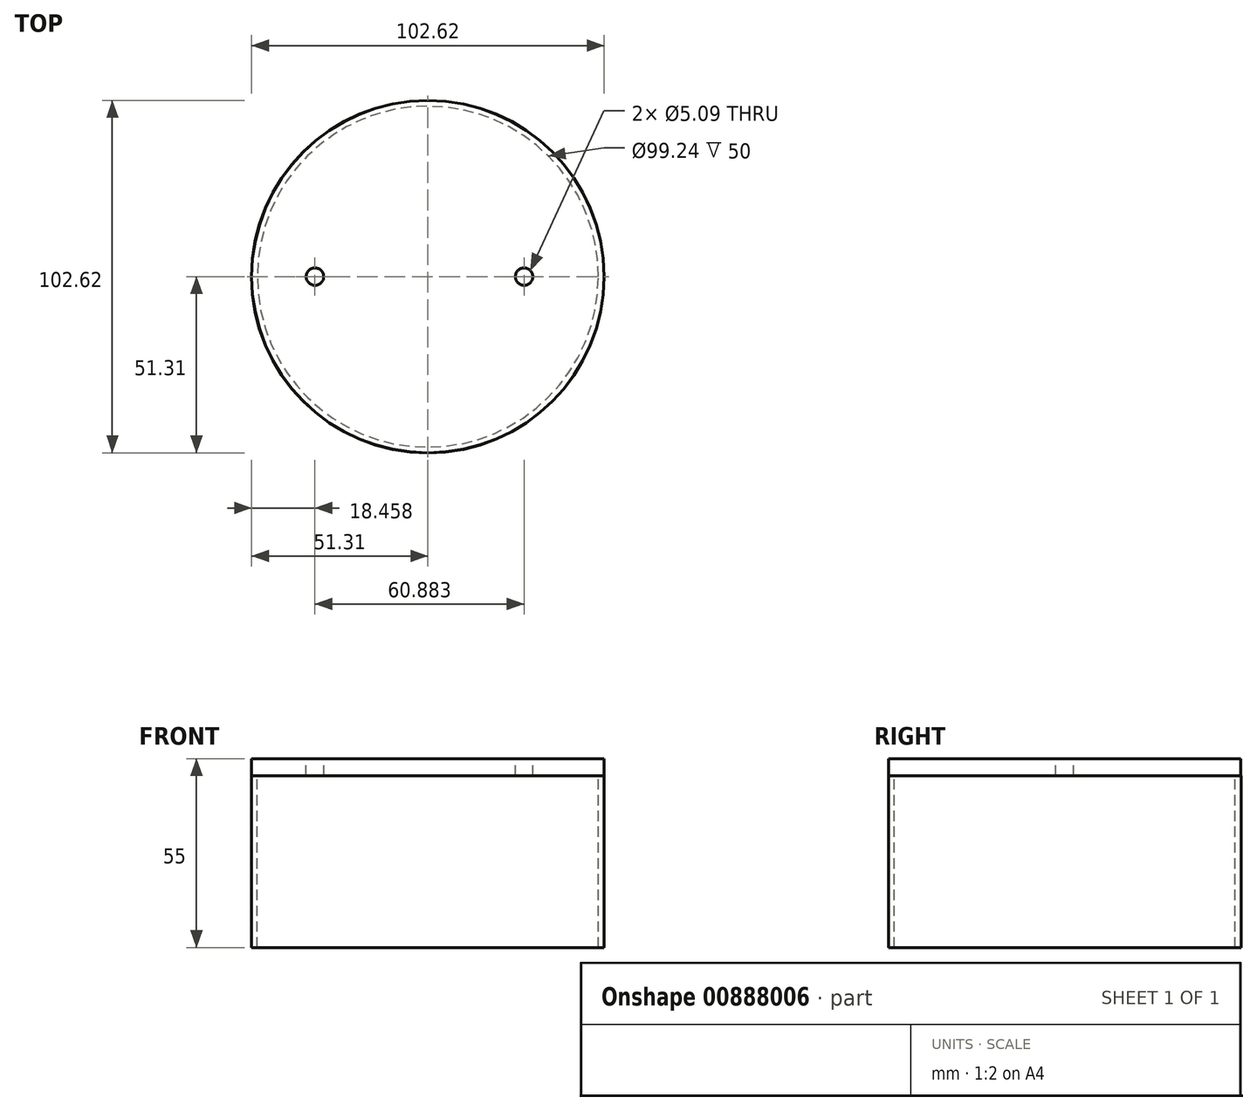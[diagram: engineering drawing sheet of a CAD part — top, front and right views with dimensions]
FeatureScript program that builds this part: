
annotation { "Feature Type Name" : "Feature", "Feature Type Description" : "" }
export const myFeature = defineFeature(function(context is Context, id is Id, definition is map)
    precondition{}
    {
        {
            var Q0;
            Q0=qCreatedBy(makeId("Top.planeOp"),FACE);
            var sketch = newSketch(context, id + "F0", { "sketchPlane" : qUnion([Q0])});
            skCircle(sketch, "E0", {"center": v(0, 0) * mm, "radius": 51.31 * mm});
            skCircle(sketch, "E1", {"center": v(0, 0) * mm, "radius": 49.62 * mm});
            skSolve(sketch);
        }
        {
            var Q0;
            Q0=makeQuery(id+"F0.imprint","IMPRINT",FACE,{"disambiguationData":[TD([[makeQuery(id+"F0.imprint","IMPRINT",EDGE,{"derivedFrom":sQuery(id+"F0.wireOp",EDGE,"E0")}),1.0]])]});
            extrude(context, id + "F1", {"entities" : qUnion([Q0]), "oppositeDirection" : true, "depth" : 50 * mm, "offsetDistance" : 25 * mm});
        }
        {
            var Q0;
            Q0=qCreatedBy(makeId("Top.planeOp"),FACE);
            var sketch = newSketch(context, id + "F2", { "sketchPlane" : qUnion([Q0])});
            skCircle(sketch, "E2", {"center": v(0, 0) * mm, "radius": 51.28 * mm});
            skSolve(sketch);
        }
        {
            var Q0;
            Q0 = qSketchRegion(id + "F2", true);
            extrude(context, id + "F3", {"entities" : qUnion([Q0]), "operationType" : NewBodyOperationType.ADD, "depth" : 5 * mm, "offsetDistance" : 25 * mm});
        }
        {
            var Q0;
            Q0=makeQuery(id+"F3.opExtrude","CAP_FACE",FACE,{"disambiguationData":[OSD([sQuery(id+"F2.wireOp",EDGE,"E2")])],"isStart":false});
            extrude(context, id + "F4", {"entities" : qUnion([Q0]), "operationType" : NewBodyOperationType.ADD, "oppositeDirection" : true, "depth" : 5 * mm, "offsetDistance" : 25 * mm});
        }
        {
            var Q0;
            Q0=makeQuery(id+"F3.opExtrude","CAP_FACE",FACE,{"disambiguationData":[OSD([sQuery(id+"F2.wireOp",EDGE,"E2")])],"isStart":false});
            var sketch = newSketch(context, id + "F5", { "sketchPlane" : qUnion([Q0])});
            skCircle(sketch, "E3", {"center": v(-32.85, 0) * mm, "radius": 2.55 * mm});
            skCircle(sketch, "E4", {"center": v(28.03, 0) * mm, "radius": 2.55 * mm});
            skSolve(sketch);
        }
        {
            var Q0;
            Q0 = qSketchRegion(id + "F5", true);
            extrude(context, id + "F6", {"entities" : qUnion([Q0]), "operationType" : NewBodyOperationType.REMOVE, "endBound" : BoundingType.THROUGH_ALL, "oppositeDirection" : true, "depth" : 25 * mm, "offsetDistance" : 25 * mm});
        }
    });
